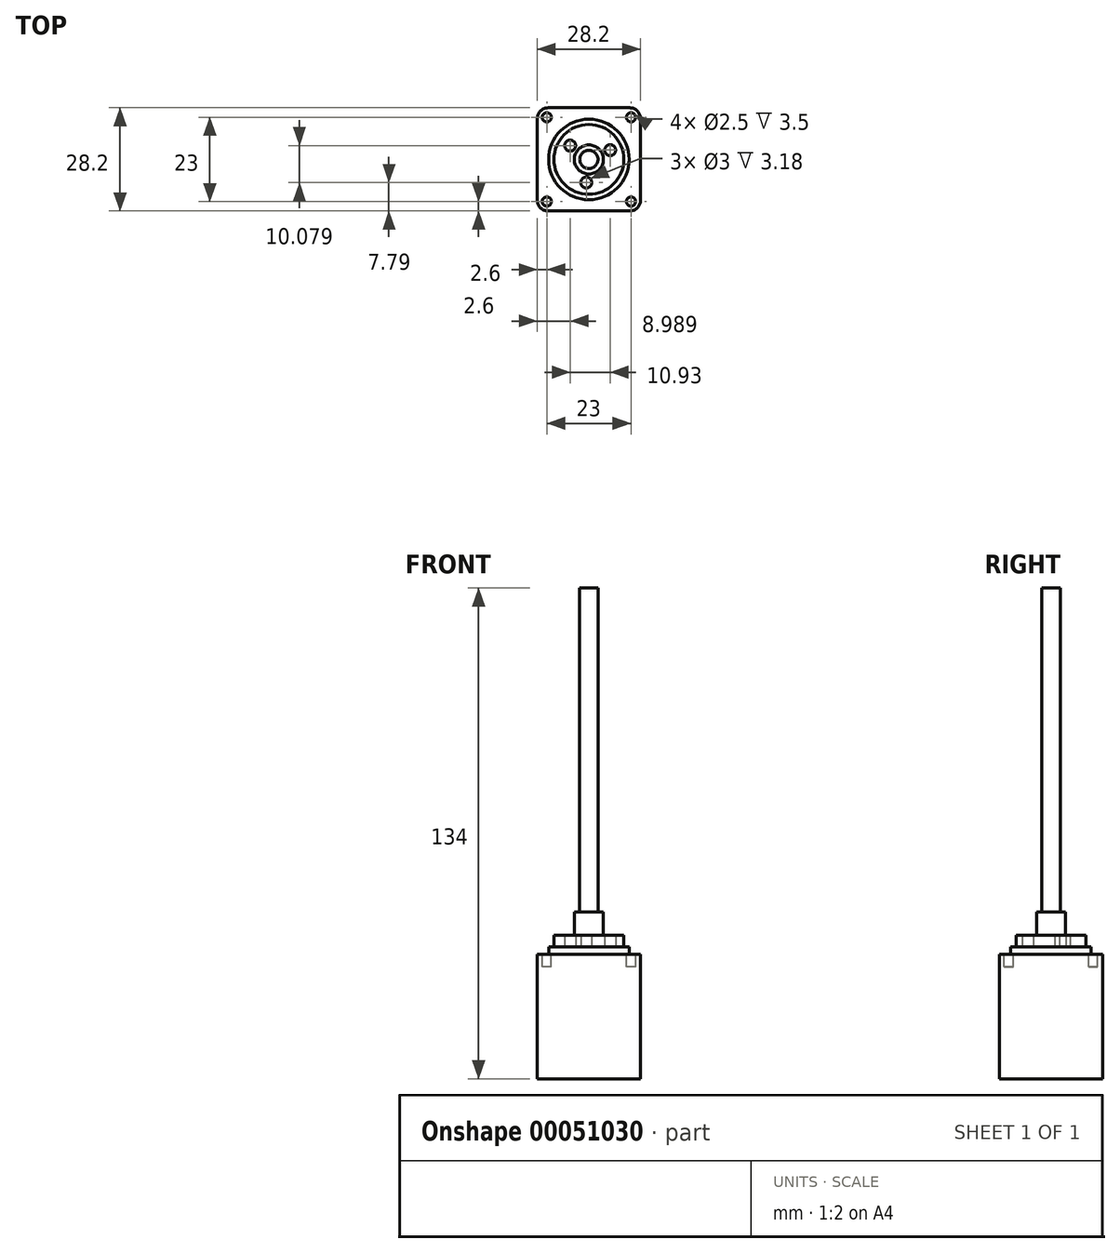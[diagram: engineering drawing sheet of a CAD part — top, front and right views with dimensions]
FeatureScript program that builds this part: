
annotation { "Feature Type Name" : "Feature", "Feature Type Description" : "" }
export const myFeature = defineFeature(function(context is Context, id is Id, definition is map)
    precondition{}
    {
        {
            var Q0;
            Q0=qCreatedBy(makeId("Front.planeOp"),FACE);
            var sketch = newSketch(context, id + "F0", { "sketchPlane" : qUnion([Q0])});
            skLineSegment(sketch, "E0.bottom", {"start": v(-14.1, 0) * mm, "end": v(14.1, 0) * mm});
            skLineSegment(sketch, "E0.top", {"start": v(-14.1, -34) * mm, "end": v(14.1, -34) * mm});
            skLineSegment(sketch, "E0.left", {"start": v(-14.1, 0) * mm, "end": v(-14.1, -34) * mm});
            skLineSegment(sketch, "E0.right", {"start": v(14.1, 0) * mm, "end": v(14.1, -34) * mm});
            skLineSegment(sketch, "E1", {"start": v(0, 54.6) * mm, "end": v(0, -51.08) * mm, "construction": true});
            skSolve(sketch);
        }
        {
            var Q0;
            Q0=makeQuery(id+"F0.imprint","IMPRINT",FACE,{"disambiguationData":[TD([[makeQuery(id+"F0.imprint","IMPRINT",EDGE,{"derivedFrom":sQuery(id+"F0.wireOp",EDGE,"E0.bottom")}),-1.0]])]});
            extrude(context, id + "F1", {"entities" : qUnion([Q0]), "endBound" : BoundingType.SYMMETRIC, "depth" : 28.2 * mm});
        }
        {
            var Q0;
            Q0=makeQuery(id+"F1.opExtrude","SWEPT_FACE",FACE,{"disambiguationData":[OSD([sQuery(id+"F0.wireOp",EDGE,"E0.bottom")])]});
            var sketch = newSketch(context, id + "F2", { "sketchPlane" : qUnion([Q0])});
            skLineSegment(sketch, "E2", {"start": v(-22.05, 0) * mm, "end": v(28.17, 0) * mm, "construction": true});
            skLineSegment(sketch, "E3", {"start": v(0, 17.29) * mm, "end": v(0, -17.48) * mm, "construction": true});
            skCircle(sketch, "E4", {"center": v(11.5, 11.5) * mm, "radius": 1.25 * mm});
            skPoint(sketch, "E5", {"position": v(0, 14.1) * mm});
            skCircle(sketch, "E6.MirrorC", {"center": v(11.5, -11.5) * mm, "radius": 1.25 * mm});
            skCircle(sketch, "E7.MirrorC", {"center": v(-11.5, -11.5) * mm, "radius": 1.25 * mm});
            skCircle(sketch, "E8.MirrorC", {"center": v(-11.5, 11.5) * mm, "radius": 1.25 * mm});
            skSolve(sketch);
        }
        {
            var Q0;
            Q0 = qSketchRegion(id + "F2", true);
            extrude(context, id + "F3", {"entities" : qUnion([Q0]), "operationType" : NewBodyOperationType.REMOVE, "oppositeDirection" : true, "depth" : 3.5 * mm});
        }
        {
            var Q0;
            Q0=makeQuery(id+"F1.opExtrude","SWEPT_FACE",FACE,{"disambiguationData":[OSD([sQuery(id+"F0.wireOp",EDGE,"E0.bottom")])]});
            var sketch = newSketch(context, id + "F4", { "sketchPlane" : qUnion([Q0])});
            skCircle(sketch, "E9", {"center": v(0, 0) * mm, "radius": 11 * mm});
            skSolve(sketch);
        }
        {
            var Q0;
            Q0 = qSketchRegion(id + "F4", true);
            extrude(context, id + "F5", {"entities" : qUnion([Q0]), "operationType" : NewBodyOperationType.ADD, "depth" : 2 * mm});
        }
        {
            var Q0;
            Q0=makeQuery(id+"F1.opExtrude","SWEPT_FACE",FACE,{"disambiguationData":[OSD([sQuery(id+"F0.wireOp",EDGE,"E0.bottom")])]});
            var sketch = newSketch(context, id + "F6", { "sketchPlane" : qUnion([Q0])});
            skCircle(sketch, "E10", {"center": v(0, 0) * mm, "radius": 2.5 * mm});
            skSolve(sketch);
        }
        {
            var Q0;
            Q0 = qSketchRegion(id + "F6", true);
            extrude(context, id + "F7", {"entities" : qUnion([Q0]), "depth" : 100 * mm});
        }
        {
            var Q0;
            Q0=makeQuery(id+"F1.opExtrude","CAP_EDGE",EDGE,{"disambiguationData":[OSD([sQuery(id+"F0.wireOp",EDGE,"E0.left")])],"isStart":true});
            var Q1;
            Q1=makeQuery(id+"F1.opExtrude","CAP_EDGE",EDGE,{"disambiguationData":[OSD([sQuery(id+"F0.wireOp",EDGE,"E0.right")])],"isStart":true});
            var Q2;
            Q2=makeQuery(id+"F1.opExtrude","CAP_EDGE",EDGE,{"disambiguationData":[OSD([sQuery(id+"F0.wireOp",EDGE,"E0.left")])],"isStart":false});
            var Q3;
            Q3=makeQuery(id+"F1.opExtrude","CAP_EDGE",EDGE,{"disambiguationData":[OSD([sQuery(id+"F0.wireOp",EDGE,"E0.right")])],"isStart":false});
            fillet(context, id + "F8", {"entities" : qUnion([Q0, Q1, Q2, Q3]), "radius" : 3 * mm, "tangentPropagation" : true, "allowEdgeOverflow" : false});
        }
        {
            var Q0;
            Q0=makeQuery(id+"F5.opExtrude","CAP_FACE",FACE,{"disambiguationData":[OSD([sQuery(id+"F4.wireOp",EDGE,"E9")])],"isStart":false});
            var sketch = newSketch(context, id + "F9", { "sketchPlane" : qUnion([Q0])});
            skCircle(sketch, "E11", {"center": v(0, 0) * mm, "radius": 9.53 * mm});
            skCircle(sketch, "E12", {"center": v(0, 0) * mm, "radius": 2.5 * mm});
            skSolve(sketch);
        }
        {
            var Q0;
            Q0 = qSketchRegion(id + "F9", true);
            extrude(context, id + "F10", {"entities" : qUnion([Q0]), "depth" : 3.18 * mm});
        }
        {
            var Q0;
            Q0=makeQuery(id+"F5.opExtrude","CAP_FACE",FACE,{"disambiguationData":[OSD([sQuery(id+"F4.wireOp",EDGE,"E9")])],"isStart":false});
            var sketch = newSketch(context, id + "F11", { "sketchPlane" : qUnion([Q0])});
            skCircle(sketch, "E13", {"center": v(0, 0) * mm, "radius": 3.97 * mm});
            skCircle(sketch, "E14", {"center": v(0, 0) * mm, "radius": 2.5 * mm});
            skSolve(sketch);
        }
        {
            var Q0;
            Q0=makeQuery(id+"F11.imprint","IMPRINT",FACE,{"disambiguationData":[TD([[makeQuery(id+"F11.imprint","IMPRINT",EDGE,{"derivedFrom":sQuery(id+"F11.wireOp",EDGE,"E13")}),1.0]])]});
            extrude(context, id + "F12", {"entities" : qUnion([Q0]), "operationType" : NewBodyOperationType.ADD, "depth" : 9.53 * mm});
        }
        {
            var Q0;
            Q0=makeQuery(id+"F5.opExtrude","CAP_FACE",FACE,{"disambiguationData":[OSD([sQuery(id+"F4.wireOp",EDGE,"E9")])],"isStart":false});
            var sketch = newSketch(context, id + "F13", { "sketchPlane" : qUnion([Q0])});
            skCircle(sketch, "E15", {"center": v(5.82, 2.54) * mm, "radius": 1.5 * mm});
            skCircle(sketch, "E16", {"center": v(0, 0) * mm, "radius": 6.35 * mm, "construction": true});
            skCircle(sketch, "E17.1.0", {"center": v(-5.11, 3.77) * mm, "radius": 1.5 * mm});
            skCircle(sketch, "E17.2.0", {"center": v(-0.7, -6.31) * mm, "radius": 1.5 * mm});
            skSolve(sketch);
        }
        {
            var Q0;
            Q0 = qSketchRegion(id + "F13", true);
            extrude(context, id + "F14", {"entities" : qUnion([Q0]), "operationType" : NewBodyOperationType.REMOVE, "endBound" : BoundingType.UP_TO_NEXT, "depth" : 25 * mm});
        }
    });
